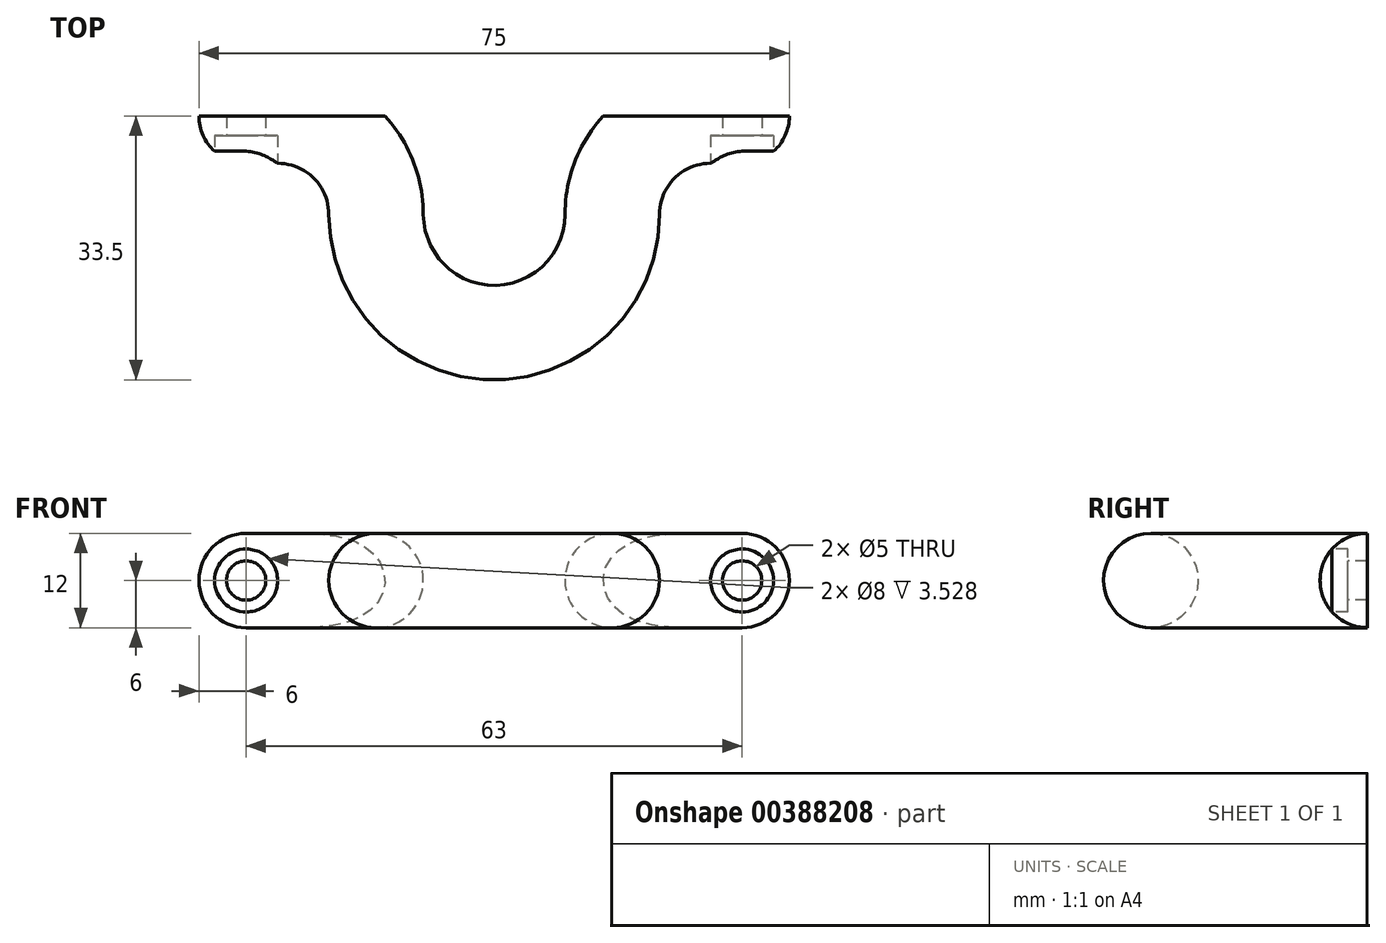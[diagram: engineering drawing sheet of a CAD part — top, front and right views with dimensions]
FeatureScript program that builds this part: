
annotation { "Feature Type Name" : "Feature", "Feature Type Description" : "" }
export const myFeature = defineFeature(function(context is Context, id is Id, definition is map)
    precondition{}
    {
        {
            var Q0;
            Q0=qCreatedBy(makeId("Top.planeOp"),FACE);
            var sketch = newSketch(context, id + "F0", { "sketchPlane" : qUnion([Q0])});
            skArc(sketch, "E0", {"start": v(-15, 0) * mm, "mid": v(0, -15) * mm, "end": v(15, 0) * mm});
            skArc(sketch, "E1", {"start": v(-15, 0) * mm, "mid": v(-18.66, 8.84) * mm, "end": v(-27.5, 12.5) * mm});
            skArc(sketch, "E2", {"start": v(27.5, 12.5) * mm, "mid": v(18.66, 8.84) * mm, "end": v(15, 0) * mm});
            skPoint(sketch, "E3", {"position": v(15, 0) * mm});
            skPoint(sketch, "E4", {"position": v(-15, 0) * mm});
            skSolve(sketch);
        }
        {
            var Q0;
            Q0=qCreatedBy(makeId("Right.planeOp"),FACE);
            cPlane(context, id + "F1", {"entities" : qUnion([Q0]), "cplaneType" : CPlaneType.OFFSET, "offset" : (15 + 12.5) * mm, "oppositeDirection" : true, "width" : 150 * mm, "height" : 150 * mm});
        }
        {
            var Q0;
            Q0=qCreatedBy(id+"F1.planeOp",FACE);
            var sketch = newSketch(context, id + "F2", { "sketchPlane" : qUnion([Q0])});
            skPoint(sketch, "E5.0", {"position": v(12.5, 0) * mm});
            skCircle(sketch, "E6", {"center": v(12.5, 0) * mm, "radius": 6 * mm});
            skSolve(sketch);
        }
        {
            var Q0;
            Q0=makeQuery(id+"F2.imprint","IMPRINT",FACE,{"disambiguationData":[TD([[makeQuery(id+"F2.imprint","IMPRINT",EDGE,{"derivedFrom":sQuery(id+"F2.wireOp",EDGE,"E6")}),1.0]])]});
            var Q1;
            Q1=sQuery(id+"F0.wireOp",EDGE,"E1");
            var Q2;
            Q2=sQuery(id+"F0.wireOp",EDGE,"E0");
            var Q3;
            Q3=sQuery(id+"F0.wireOp",EDGE,"E2");
            sweep(context, id + "F3", {"profiles" : qUnion([Q0]), "path" : qUnion([Q1, Q2, Q3])});
        }
        {
            var Q0;
            Q0=makeQuery(id+"F3.opSweep","CAP_FACE",FACE,{"disambiguationData":[OSD([sQuery(id+"F0.wireOp",VERTEX,"E2.start"),sQuery(id+"F2.wireOp",EDGE,"E6")])],"isStart":false});
            extrude(context, id + "F4", {"entities" : qUnion([Q0]), "operationType" : NewBodyOperationType.ADD, "depth" : 10 * mm});
        }
        {
            var Q0;
            Q0=makeQuery(id+"F3.opSweep","CAP_FACE",FACE,{"disambiguationData":[OSD([sQuery(id+"F0.wireOp",VERTEX,"E1.end"),sQuery(id+"F2.wireOp",EDGE,"E6")])],"isStart":true});
            extrude(context, id + "F5", {"entities" : qUnion([Q0]), "operationType" : NewBodyOperationType.ADD, "depth" : 10 * mm});
        }
        {
            var Q0;
            Q0=qCreatedBy(makeId("Front.planeOp"),FACE);
            cPlane(context, id + "F6", {"entities" : qUnion([Q0]), "cplaneType" : CPlaneType.OFFSET, "offset" : 12.5 * mm, "oppositeDirection" : true, "width" : 150 * mm, "height" : 150 * mm});
        }
        {
            var Q0;
            Q0=qCreatedBy(makeId("Top.planeOp"),FACE);
            cPlane(context, id + "F7", {"entities" : qUnion([Q0]), "cplaneType" : CPlaneType.OFFSET, "offset" : 6 * mm, "width" : 150 * mm, "height" : 150 * mm});
        }
        {
            var Q0;
            Q0=makeQuery(id+"F5.opExtrude","CAP_FACE",FACE,{"disambiguationData":[OSD([sQuery(id+"F0.wireOp",VERTEX,"E1.end"),sQuery(id+"F2.wireOp",EDGE,"E6")])],"isStart":false});
            var sketch = newSketch(context, id + "F8", { "sketchPlane" : qUnion([Q0])});
            skPoint(sketch, "E7", {"position": v(-12.5, 0) * mm});
            skPoint(sketch, "E8", {"position": v(-12.5, 6) * mm});
            skSolve(sketch);
        }
        {
            var Q0;
            Q0=qCreatedBy(id+"F7.planeOp",FACE);
            var sketch = newSketch(context, id + "F9", { "sketchPlane" : qUnion([Q0])});
            skPoint(sketch, "E9.0", {"position": v(-37.5, 12.5) * mm});
            skLineSegment(sketch, "E10.bottom", {"start": v(-37.5, 12.5) * mm, "end": v(48.36, 12.5) * mm});
            skLineSegment(sketch, "E10.top", {"start": v(-37.5, 29.7) * mm, "end": v(48.36, 29.7) * mm});
            skLineSegment(sketch, "E10.left", {"start": v(-37.5, 12.5) * mm, "end": v(-37.5, 29.7) * mm});
            skLineSegment(sketch, "E10.right", {"start": v(48.36, 12.5) * mm, "end": v(48.36, 29.7) * mm});
            skSolve(sketch);
        }
        {
            var Q0;
            Q0 = qSketchRegion(id + "F9", true);
            extrude(context, id + "F10", {"entities" : qUnion([Q0]), "operationType" : NewBodyOperationType.REMOVE, "oppositeDirection" : true, "depth" : 25 * mm});
        }
        {
            var Q0;
            Q0=makeQuery(id+"F4.opExtrude","CAP_EDGE",EDGE,{"disambiguationData":[OSD([sQuery(id+"F0.wireOp",VERTEX,"E2.start"),sQuery(id+"F2.wireOp",EDGE,"E6")])],"isStart":false});
            var Q1;
            Q1=makeQuery(id+"F5.opExtrude","CAP_EDGE",EDGE,{"disambiguationData":[OSD([sQuery(id+"F0.wireOp",VERTEX,"E1.end"),sQuery(id+"F2.wireOp",EDGE,"E6")])],"isStart":false});
            fillet(context, id + "F11", {"entities" : qUnion([Q0, Q1]), "radius" : 6 * mm, "tangentPropagation" : true, "allowEdgeOverflow" : false});
        }
        {
            var Q0;
            Q0=qCreatedBy(id+"F6.planeOp",FACE);
            cPlane(context, id + "F12", {"entities" : qUnion([Q0]), "cplaneType" : CPlaneType.OFFSET, "offset" : 6 * mm, "width" : 150 * mm, "height" : 150 * mm});
        }
        {
            var Q0;
            Q0=qCreatedBy(id+"F12.planeOp",FACE);
            var sketch = newSketch(context, id + "F13", { "sketchPlane" : qUnion([Q0])});
            skPoint(sketch, "E11.0", {"position": v(-37.5, 0) * mm});
            skPoint(sketch, "E12.0", {"position": v(37.5, 0) * mm});
            skPoint(sketch, "E13", {"position": v(-31.5, 0) * mm});
            skPoint(sketch, "E14", {"position": v(31.5, 0) * mm});
            skSolve(sketch);
        }
        {
            var Q0;
            Q0=sQuery(id+"F13.wireOp",VERTEX,"E13");
            var Q1;
            Q1=sQuery(id+"F13.wireOp",VERTEX,"E14");
            var Q2;
            Q2=makeQuery(id+"F3.opSweep","SWEPT_BODY",BODY,{"disambiguationData":[OSD([sQuery(id+"F0.wireOp",EDGE,"E2"),sQuery(id+"F2.wireOp",EDGE,"E6")])]});
            hole(context, id + "F14", {"style" : HoleStyle.C_BORE, "endStyle" : HoleEndStyle.THROUGH, "holeDiameter" : 5 * mm, "cBoreDiameter" : 8 * mm, "cBoreDepth" : 2 * mm, "isTappedThrough" : true, "tappedDepth" : 12 * mm, "tapClearance" : 3, "locations" : qUnion([Q0, Q1]), "scope" : qUnion([Q2])});
        }
    });
